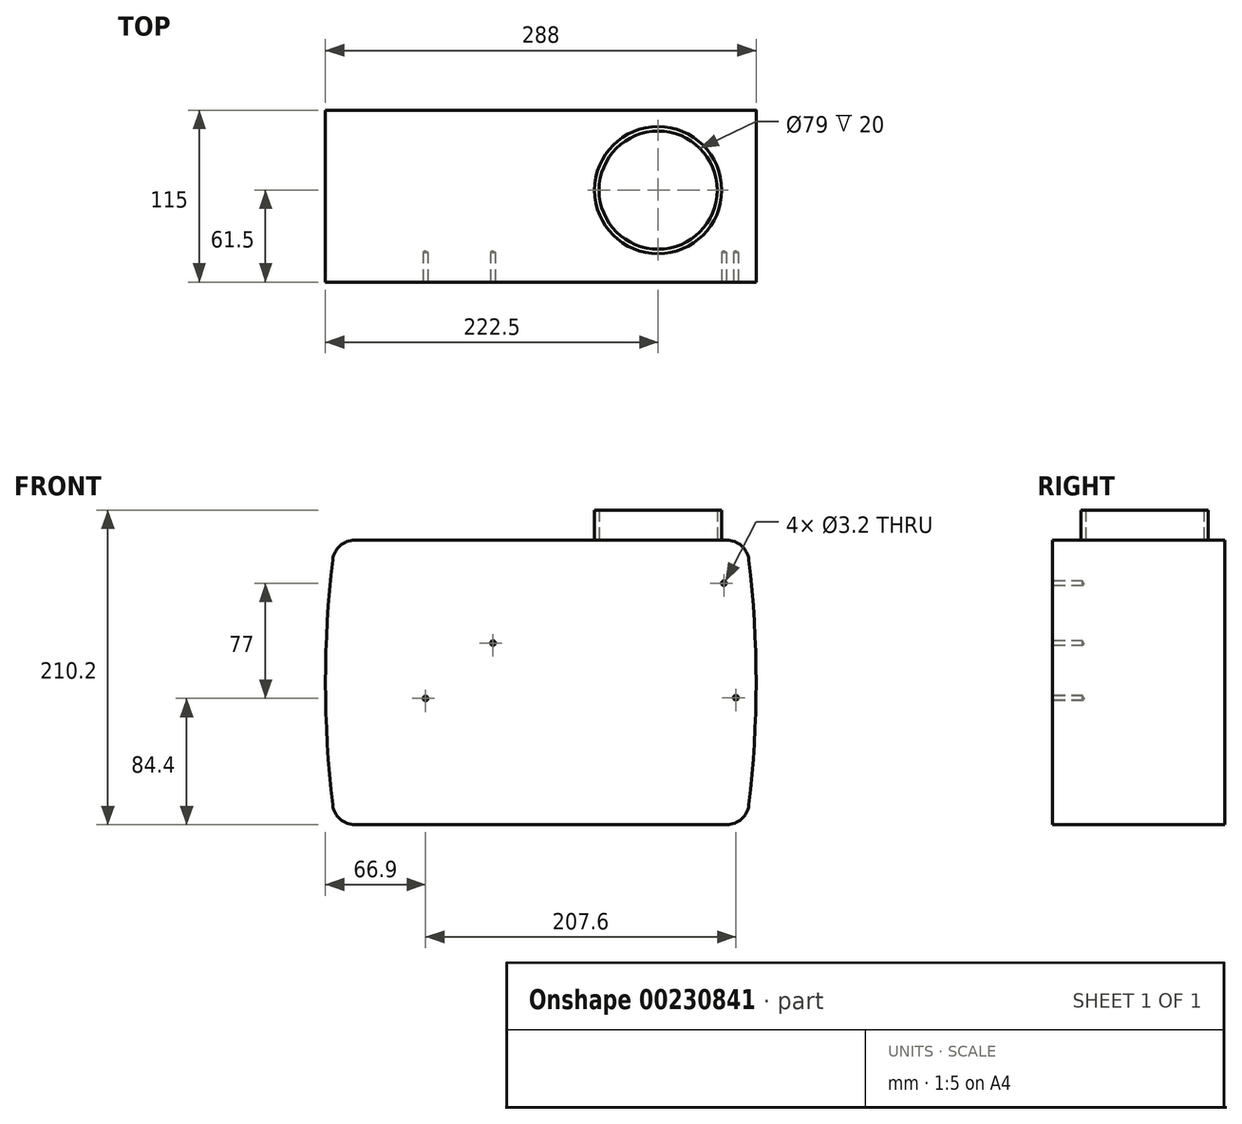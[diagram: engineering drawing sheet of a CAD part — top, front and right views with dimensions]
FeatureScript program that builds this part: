
annotation { "Feature Type Name" : "Feature", "Feature Type Description" : "" }
export const myFeature = defineFeature(function(context is Context, id is Id, definition is map)
    precondition{}
    {
        {
            var Q0;
            Q0=qCreatedBy(makeId("Front.planeOp"),FACE);
            var sketch = newSketch(context, id + "F0", { "sketchPlane" : qUnion([Q0])});
            skLineSegment(sketch, "E0", {"start": v(13.2, 0) * mm, "end": v(261.81, 0) * mm});
            skLineSegment(sketch, "E1", {"start": v(13.2, 190.2) * mm, "end": v(261.81, 190.2) * mm});
            skArc(sketch, "E2", {"start": v(-1.69, 176.95) * mm, "mid": v(-6.5, 95.1) * mm, "end": v(-1.69, 13.25) * mm});
            skArc(sketch, "E3", {"start": v(276.7, 13.25) * mm, "mid": v(281.5, 95.1) * mm, "end": v(276.7, 176.95) * mm});
            skLineSegment(sketch, "E4", {"start": v(-6.5, 308.07) * mm, "end": v(-6.5, -283.02) * mm, "construction": true});
            skPoint(sketch, "E5.visualSharp", {"position": v(0, 190.2) * mm});
            skArc(sketch, "E5.filletArc", {"start": v(13.2, 190.2) * mm, "mid": v(3.24, 186.4) * mm, "end": v(-1.69, 176.95) * mm});
            skPoint(sketch, "E6.visualSharp", {"position": v(275.02, 190.2) * mm});
            skArc(sketch, "E6.filletArc", {"start": v(276.7, 176.95) * mm, "mid": v(271.78, 186.4) * mm, "end": v(261.81, 190.2) * mm});
            skPoint(sketch, "E7.visualSharp", {"position": v(275.02, 0) * mm});
            skArc(sketch, "E7.filletArc", {"start": v(261.81, 0) * mm, "mid": v(271.78, 3.8) * mm, "end": v(276.7, 13.25) * mm});
            skPoint(sketch, "E8.visualSharp", {"position": v(0, 0) * mm});
            skArc(sketch, "E8.filletArc", {"start": v(-1.69, 13.25) * mm, "mid": v(3.24, 3.8) * mm, "end": v(13.2, 0) * mm});
            skPoint(sketch, "E9", {"position": v(60.4, 84.4) * mm});
            skPoint(sketch, "E10", {"position": v(105.5, 121.4) * mm});
            skPoint(sketch, "E11", {"position": v(260, 161.4) * mm});
            skPoint(sketch, "E12", {"position": v(268, 84.9) * mm});
            skLineSegment(sketch, "E13", {"start": v(281.5, 283.78) * mm, "end": v(281.5, -191.71) * mm, "construction": true});
            skSolve(sketch);
        }
        {
            var Q0;
            Q0=makeQuery(id+"F0.imprint","IMPRINT",FACE,{"disambiguationData":[TD([[makeQuery(id+"F0.imprint","IMPRINT",EDGE,{"derivedFrom":sQuery(id+"F0.wireOp",EDGE,"E0")}),1.0]])]});
            extrude(context, id + "F1", {"entities" : qUnion([Q0]), "oppositeDirection" : true, "depth" : 115 * mm});
        }
        {
            var Q0;
            Q0=sQuery(id+"F0.wireOp",VERTEX,"E9");
            var Q1;
            Q1=sQuery(id+"F0.wireOp",VERTEX,"E10");
            var Q2;
            Q2=sQuery(id+"F0.wireOp",VERTEX,"E12");
            var Q3;
            Q3=sQuery(id+"F0.wireOp",VERTEX,"E11");
            var Q4;
            Q4=makeQuery(id+"F1.opExtrude","SWEPT_BODY",BODY,{"disambiguationData":[OSD([sQuery(id+"F0.wireOp",EDGE,"E0"),sQuery(id+"F0.wireOp",EDGE,"E1"),sQuery(id+"F0.wireOp",EDGE,"E2"),sQuery(id+"F0.wireOp",EDGE,"E3"),sQuery(id+"F0.wireOp",EDGE,"E5.filletArc"),sQuery(id+"F0.wireOp",EDGE,"E6.filletArc"),sQuery(id+"F0.wireOp",EDGE,"E7.filletArc"),sQuery(id+"F0.wireOp",EDGE,"E8.filletArc")])]});
            hole(context, id + "F2", {"style" : HoleStyle.SIMPLE, "endStyle" : HoleEndStyle.BLIND, "standardTappedOrClearance" : lookupTablePath({ "standard" : "ISO", "fit" : "Normal", "engagement" : "75%", "pitch" : "0.75 mm", "size" : "M4", "type" : "Tapped" }), "standardBlindInLast" : lookupTablePath({ "fit" : "Free", "standard" : "ISO", "engagement" : "75%", "pitch" : "0.75 mm", "size" : "M4", "type" : "Tapped" }), "holeDiameter" : 3.2 * mm, "holeDepth" : 20 * mm, "locations" : qUnion([Q0, Q1, Q2, Q3]), "scope" : qUnion([Q4])});
        }
        {
            var Q0;
            Q0=makeQuery(id+"F1.opExtrude","SWEPT_FACE",FACE,{"disambiguationData":[OSD([sQuery(id+"F0.wireOp",EDGE,"E1")])]});
            var sketch = newSketch(context, id + "F3", { "sketchPlane" : qUnion([Q0])});
            skCircle(sketch, "E14", {"center": v(216, 61.5) * mm, "radius": 39.5 * mm});
            skCircle(sketch, "E15", {"center": v(216, 61.5) * mm, "radius": 42.5 * mm});
            skLineSegment(sketch, "E16", {"start": v(281.5, 0) * mm, "end": v(281.5, -92) * mm, "construction": true});
            skSolve(sketch);
        }
        {
            var Q0;
            Q0 = qSketchRegion(id + "F3", true);
            extrude(context, id + "F4", {"entities" : qUnion([Q0]), "operationType" : NewBodyOperationType.ADD, "depth" : 20 * mm});
        }
    });
